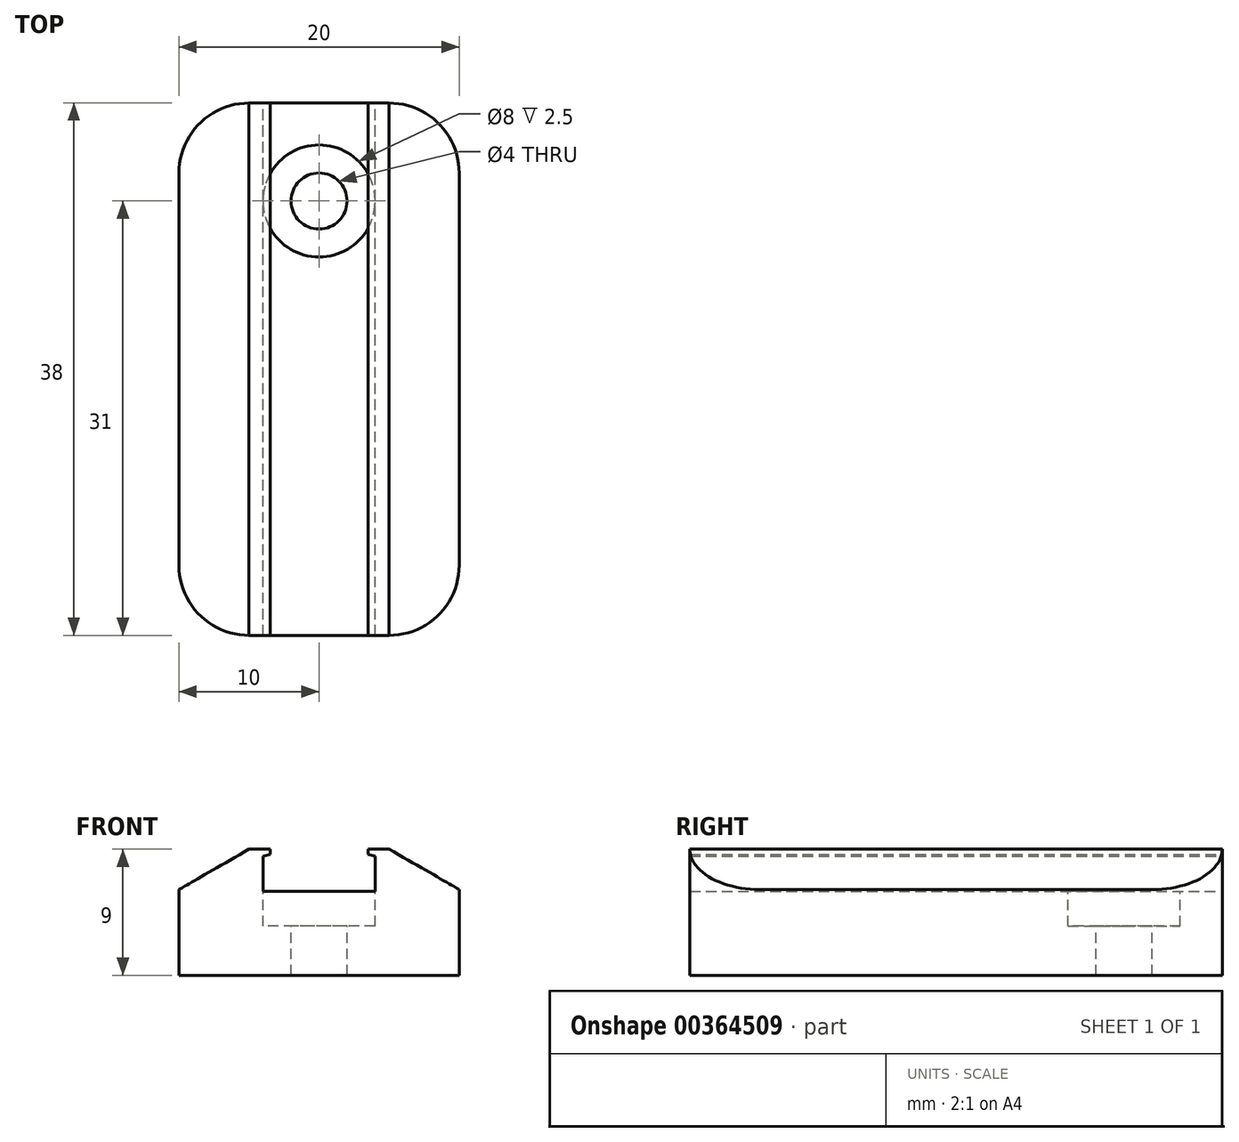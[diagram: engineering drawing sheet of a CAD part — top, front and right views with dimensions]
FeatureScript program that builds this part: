
annotation { "Feature Type Name" : "Feature", "Feature Type Description" : "" }
export const myFeature = defineFeature(function(context is Context, id is Id, definition is map)
    precondition{}
    {
        {
            var Q0;
            Q0=qCreatedBy(makeId("Front.planeOp"),FACE);
            var sketch = newSketch(context, id + "F0", { "sketchPlane" : qUnion([Q0])});
            skLineSegment(sketch, "E0", {"start": v(0, 0) * mm, "end": v(10, 0) * mm});
            skLineSegment(sketch, "E1", {"start": v(10, 0) * mm, "end": v(10, 9) * mm});
            skLineSegment(sketch, "E2", {"start": v(10, 9) * mm, "end": v(3.5, 9) * mm});
            skLineSegment(sketch, "E3", {"start": v(3.5, 9) * mm, "end": v(3.5, 8.63) * mm});
            skLineSegment(sketch, "E4", {"start": v(3.5, 8.63) * mm, "end": v(4, 8.5) * mm});
            skLineSegment(sketch, "E5", {"start": v(4, 8.5) * mm, "end": v(4, 6) * mm});
            skLineSegment(sketch, "E6", {"start": v(4, 6) * mm, "end": v(0, 6) * mm});
            skLineSegment(sketch, "E7", {"start": v(0, 6) * mm, "end": v(0, 0) * mm, "construction": true});
            skLineSegment(sketch, "E8.MirrorCS", {"start": v(-10, 9) * mm, "end": v(-3.5, 9) * mm});
            skLineSegment(sketch, "E9.MirrorCS", {"start": v(-4, 8.5) * mm, "end": v(-4, 6) * mm});
            skLineSegment(sketch, "E10.MirrorCS", {"start": v(-3.5, 8.63) * mm, "end": v(-4, 8.5) * mm});
            skLineSegment(sketch, "E11.MirrorCS", {"start": v(-3.5, 9) * mm, "end": v(-3.5, 8.63) * mm});
            skLineSegment(sketch, "E12.MirrorCS", {"start": v(-10, 0) * mm, "end": v(-10, 9) * mm});
            skLineSegment(sketch, "E13.MirrorCS", {"start": v(0, 0) * mm, "end": v(-10, 0) * mm});
            skLineSegment(sketch, "E14.MirrorCS", {"start": v(-4, 6) * mm, "end": v(0, 6) * mm});
            skSolve(sketch);
        }
        {
            var Q0;
            Q0 = qSketchRegion(id + "F0", true);
            extrude(context, id + "F1", {"entities" : qUnion([Q0]), "endBound" : BoundingType.SYMMETRIC, "depth" : 38 * mm});
        }
        {
            var Q0;
            Q0=makeQuery(id+"F1.opExtrude","SWEPT_EDGE",EDGE,{"disambiguationData":[OSD([sQuery(id+"F0.wireOp",EDGE,"E8.MirrorCS"),sQuery(id+"F0.wireOp",EDGE,"E12.MirrorCS")])]});
            chamfer(context, id + "F2", {"entities" : qUnion([Q0]), "chamferType" : ChamferType.OFFSET_ANGLE, "width" : 5 * mm, "oppositeDirection" : true, "angle" : 30 * degree, "tangentPropagation" : true});
        }
        {
            var Q0;
            Q0=makeQuery(id+"F1.opExtrude","SWEPT_EDGE",EDGE,{"disambiguationData":[OSD([sQuery(id+"F0.wireOp",EDGE,"E1"),sQuery(id+"F0.wireOp",EDGE,"E2")])]});
            chamfer(context, id + "F3", {"entities" : qUnion([Q0]), "chamferType" : ChamferType.OFFSET_ANGLE, "width" : 5 * mm, "oppositeDirection" : false, "angle" : 30 * degree, "tangentPropagation" : true});
        }
        {
            var Q0;
            Q0=makeQuery(id+"F1.opExtrude","SWEPT_FACE",FACE,{"disambiguationData":[OSD([sQuery(id+"F0.wireOp",EDGE,"E6"),sQuery(id+"F0.wireOp",EDGE,"E14.MirrorCS")])]});
            var sketch = newSketch(context, id + "F4", { "sketchPlane" : qUnion([Q0])});
            skCircle(sketch, "E15", {"center": v(0, 12) * mm, "radius": 4 * mm});
            skLineSegment(sketch, "E16", {"start": v(0, 12) * mm, "end": v(0, 0) * mm, "construction": true});
            skSolve(sketch);
        }
        {
            var Q0;
            Q0 = qSketchRegion(id + "F4", true);
            extrude(context, id + "F5", {"entities" : qUnion([Q0]), "operationType" : NewBodyOperationType.REMOVE, "oppositeDirection" : true, "depth" : 2.5 * mm});
        }
        {
            var Q0;
            Q0=makeQuery(id+"F5.boolean.opBoolean","COPY",FACE,{"derivedFrom":makeQuery(id+"F5.opExtrude","CAP_FACE",FACE,{"disambiguationData":[OSD([sQuery(id+"F4.wireOp",EDGE,"E15")])],"isStart":false})});
            var sketch = newSketch(context, id + "F6", { "sketchPlane" : qUnion([Q0])});
            skCircle(sketch, "E17", {"center": v(0, 12) * mm, "radius": 2 * mm});
            skSolve(sketch);
        }
        {
            var Q0;
            Q0 = qSketchRegion(id + "F6", true);
            extrude(context, id + "F7", {"entities" : qUnion([Q0]), "operationType" : NewBodyOperationType.REMOVE, "endBound" : BoundingType.UP_TO_NEXT, "oppositeDirection" : true, "depth" : 25 * mm});
        }
        {
            var Q0;
            Q0=makeQuery(id+"F1.opExtrude","CAP_EDGE",EDGE,{"disambiguationData":[OSD([sQuery(id+"F0.wireOp",EDGE,"E12.MirrorCS")])],"isStart":true});
            var Q1;
            Q1=makeQuery(id+"F1.opExtrude","CAP_EDGE",EDGE,{"disambiguationData":[OSD([sQuery(id+"F0.wireOp",EDGE,"E12.MirrorCS")])],"isStart":false});
            var Q2;
            Q2=makeQuery(id+"F1.opExtrude","CAP_EDGE",EDGE,{"disambiguationData":[OSD([sQuery(id+"F0.wireOp",EDGE,"E1")])],"isStart":false});
            var Q3;
            Q3=makeQuery(id+"F1.opExtrude","CAP_EDGE",EDGE,{"disambiguationData":[OSD([sQuery(id+"F0.wireOp",EDGE,"E1")])],"isStart":true});
            fillet(context, id + "F8", {"entities" : qUnion([Q0, Q1, Q2, Q3]), "radius" : 5 * mm, "tangentPropagation" : true, "allowEdgeOverflow" : false});
        }
    });
